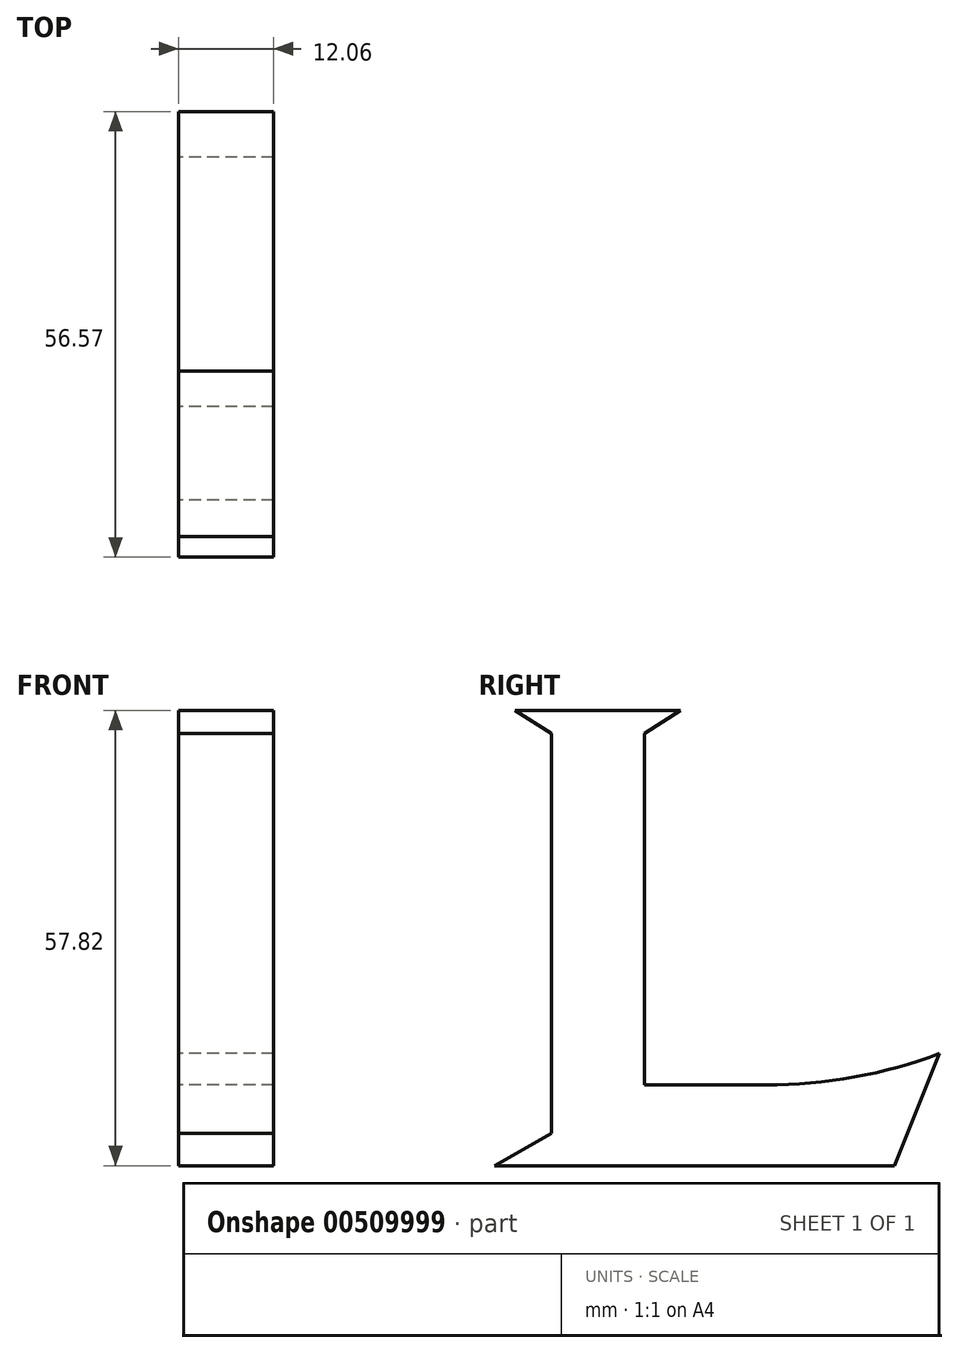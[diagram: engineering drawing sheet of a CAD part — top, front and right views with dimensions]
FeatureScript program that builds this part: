
annotation { "Feature Type Name" : "Feature", "Feature Type Description" : "" }
export const myFeature = defineFeature(function(context is Context, id is Id, definition is map)
    precondition{}
    {
        {
            var Q0;
            Q0=qCreatedBy(makeId("Right.planeOp"),FACE);
            var sketch = newSketch(context, id + "F0", { "sketchPlane" : qUnion([Q0])});
            skLineSegment(sketch, "E0", {"start": v(-7.24, 0) * mm, "end": v(43.56, 0) * mm});
            skLineSegment(sketch, "E1", {"start": v(-7.24, 0) * mm, "end": v(0, 4.13) * mm});
            skLineSegment(sketch, "E2", {"start": v(0, 4.13) * mm, "end": v(0, 54.93) * mm});
            skLineSegment(sketch, "E3", {"start": v(0, 54.93) * mm, "end": v(-4.62, 57.82) * mm});
            skLineSegment(sketch, "E4", {"start": v(-4.62, 57.82) * mm, "end": v(16.37, 57.82) * mm});
            skLineSegment(sketch, "E5", {"start": v(16.37, 57.82) * mm, "end": v(11.85, 54.9) * mm});
            skLineSegment(sketch, "E6", {"start": v(11.85, 54.9) * mm, "end": v(11.85, 10.25) * mm});
            skLineSegment(sketch, "E7", {"start": v(11.85, 10.25) * mm, "end": v(27.27, 10.25) * mm});
            skArc(sketch, "E8", {"start": v(27.27, 10.25) * mm, "mid": v(38.48, 11.25) * mm, "end": v(49.33, 14.23) * mm});
            skLineSegment(sketch, "E9", {"start": v(49.33, 14.23) * mm, "end": v(43.56, 0) * mm});
            skLineSegment(sketch, "E10", {"start": v(-4.62, 57.82) * mm, "end": v(-32.7, 57.82) * mm, "construction": true});
            skLineSegment(sketch, "E11", {"start": v(-32.7, 57.82) * mm, "end": v(-32.7, 0) * mm, "construction": true});
            skLineSegment(sketch, "E12", {"start": v(49.33, 14.23) * mm, "end": v(49.33, -22.32) * mm, "construction": true});
            skLineSegment(sketch, "E13", {"start": v(-7.24, 0) * mm, "end": v(-7.24, -22.1) * mm, "construction": true});
            skLineSegment(sketch, "E14", {"start": v(-7.24, -22.1) * mm, "end": v(49.33, -22.32) * mm, "construction": true});
            skSolve(sketch);
        }
        {
            var Q0;
            Q0=makeQuery(id+"F0.imprint","IMPRINT",FACE,{"disambiguationData":[TD([[makeQuery(id+"F0.imprint","IMPRINT",EDGE,{"derivedFrom":sQuery(id+"F0.wireOp",EDGE,"E0")}),1.0]])]});
            extrude(context, id + "F1", {"entities" : qUnion([Q0]), "depth" : 12.06 * mm});
        }
        {
            var Q0;
            Q0=qCreatedBy(makeId("Right.planeOp"),FACE);
            var sketch = newSketch(context, id + "F2", { "sketchPlane" : qUnion([Q0])});
            skLineSegment(sketch, "E15", {"start": v(-10.25, -3.03) * mm, "end": v(53.25, -3.03) * mm});
            skLineSegment(sketch, "E16", {"start": v(53.25, -3.03) * mm, "end": v(53.25, 60.47) * mm});
            skLineSegment(sketch, "E17", {"start": v(53.25, 60.47) * mm, "end": v(-10.25, 60.47) * mm});
            skLineSegment(sketch, "E18", {"start": v(-10.25, 60.47) * mm, "end": v(-10.25, -3.03) * mm});
            skLineSegment(sketch, "E19", {"start": v(-8.85, -1.59) * mm, "end": v(-8.85, 58.82) * mm});
            skLineSegment(sketch, "E20", {"start": v(-8.85, 58.82) * mm, "end": v(51.56, 58.82) * mm});
            skLineSegment(sketch, "E21", {"start": v(51.56, 58.82) * mm, "end": v(51.56, -1.42) * mm});
            skLineSegment(sketch, "E22", {"start": v(51.56, -1.42) * mm, "end": v(-8.85, -1.59) * mm});
            skLineSegment(sketch, "E23", {"start": v(-10.25, 60.47) * mm, "end": v(-8.85, 58.82) * mm});
            skLineSegment(sketch, "E24", {"start": v(-8.85, -1.59) * mm, "end": v(-10.25, -3.03) * mm});
            skLineSegment(sketch, "E25", {"start": v(51.56, -1.42) * mm, "end": v(53.25, -3.03) * mm});
            skLineSegment(sketch, "E26", {"start": v(51.56, 58.82) * mm, "end": v(53.25, 60.47) * mm});
            skSolve(sketch);
        }
        {
            var Q0;
            Q0=qSketchRegion(id+"F2",true);
            extrude(context, id + "F3", {"entities" : qUnion([Q0]), "depth" : 12.24 * mm});
        }
        {
            var Q0;
            Q0=qCreatedBy(makeId("Right.planeOp"),FACE);
            var sketch = newSketch(context, id + "F4", { "sketchPlane" : qUnion([Q0])});
            skLineSegment(sketch, "E27.bottom", {"start": v(-10.4, 60.5) * mm, "end": v(53.46, 60.5) * mm});
            skLineSegment(sketch, "E27.top", {"start": v(-10.4, -3.15) * mm, "end": v(53.46, -3.15) * mm});
            skLineSegment(sketch, "E27.left", {"start": v(-10.4, 60.5) * mm, "end": v(-10.4, -3.15) * mm});
            skLineSegment(sketch, "E27.right", {"start": v(53.46, 60.5) * mm, "end": v(53.46, -3.15) * mm});
            skSolve(sketch);
        }
        {
            var Q0;
            Q0=qSketchRegion(id+"F4",true);
            extrude(context, id + "F5", {"entities" : qUnion([Q0]), "oppositeDirection" : true, "depth" : 2.13 * mm});
        }
        {
            var Q0;
            Q0=makeQuery(id+"F5.opExtrude","CAP_FACE",FACE,{"disambiguationData":[OSD([sQuery(id+"F4.wireOp",EDGE,"E27.bottom"),sQuery(id+"F4.wireOp",EDGE,"E27.top"),sQuery(id+"F4.wireOp",EDGE,"E27.left"),sQuery(id+"F4.wireOp",EDGE,"E27.right")])],"isStart":false});
            var sketch = newSketch(context, id + "F6", { "sketchPlane" : qUnion([Q0])});
            skLineSegment(sketch, "E28.bottom", {"start": v(-53.46, 60.5) * mm, "end": v(10.4, 60.5) * mm});
            skLineSegment(sketch, "E28.top", {"start": v(-53.46, -3.15) * mm, "end": v(10.4, -3.15) * mm});
            skLineSegment(sketch, "E28.left", {"start": v(-53.46, 60.5) * mm, "end": v(-53.46, -3.15) * mm});
            skLineSegment(sketch, "E28.right", {"start": v(10.4, 60.5) * mm, "end": v(10.4, -3.15) * mm});
            skPoint(sketch, "E29.centerSnap0", {"position": v(10.4, 28.68) * mm});
            skPoint(sketch, "E29.centerSnap1", {"position": v(-21.53, 60.5) * mm});
            skCircle(sketch, "E30", {"center": v(-21.53, 28.68) * mm, "radius": 49 * mm});
            skSolve(sketch);
        }
        {
            var Q0;
            Q0=makeQuery(id+"F6.imprint","IMPRINT",FACE,{"disambiguationData":[TD([[makeQuery(id+"F6.imprint","IMPRINT",EDGE,{"derivedFrom":sQuery(id+"F6.wireOp",EDGE,"E28.bottom")}),-1.0]])]});
            extrude(context, id + "F7", {"entities" : qUnion([Q0]), "operationType" : NewBodyOperationType.ADD, "oppositeDirection" : true, "depth" : 9.14 * mm});
        }
        {
            var Q0;
            Q0=makeQuery(id+"F3.opExtrude","SWEPT_BODY",BODY,{"disambiguationData":[OSD([sQuery(id+"F2.wireOp",EDGE,"E15"),sQuery(id+"F2.wireOp",EDGE,"E16"),sQuery(id+"F2.wireOp",EDGE,"E17"),sQuery(id+"F2.wireOp",EDGE,"E18"),sQuery(id+"F2.wireOp",EDGE,"E19"),sQuery(id+"F2.wireOp",EDGE,"E20"),sQuery(id+"F2.wireOp",EDGE,"E21"),sQuery(id+"F2.wireOp",EDGE,"E22")])]});
            var Q1;
            Q1=makeQuery(id+"F5.opExtrude","SWEPT_BODY",BODY,{"disambiguationData":[OSD([sQuery(id+"F4.wireOp",EDGE,"E27.bottom"),sQuery(id+"F4.wireOp",EDGE,"E27.top"),sQuery(id+"F4.wireOp",EDGE,"E27.left"),sQuery(id+"F4.wireOp",EDGE,"E27.right")])]});
            deleteBodies(context, id + "F8", {"entities" : qUnion([Q0, Q1])});
        }
    });
